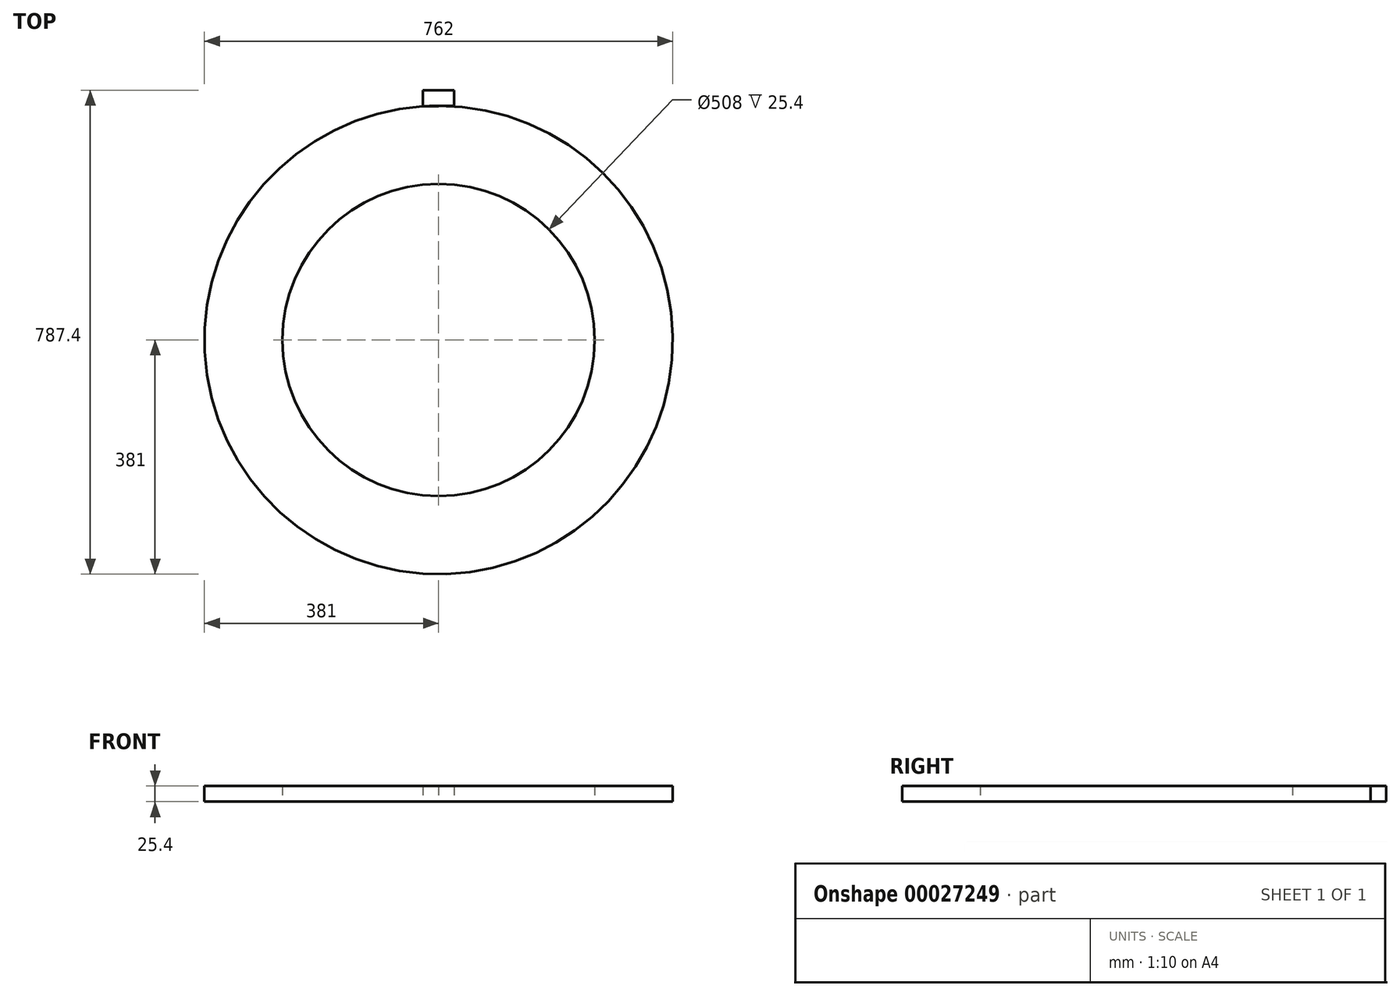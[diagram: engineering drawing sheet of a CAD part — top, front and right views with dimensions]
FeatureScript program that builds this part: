
annotation { "Feature Type Name" : "Feature", "Feature Type Description" : "" }
export const myFeature = defineFeature(function(context is Context, id is Id, definition is map)
    precondition{}
    {
        {
            var Q0;
            Q0=qCreatedBy(makeId("Top.planeOp"),FACE);
            var sketch = newSketch(context, id + "F0", { "sketchPlane" : qUnion([Q0])});
            skCircle(sketch, "E0", {"center": v(0, 0) * mm, "radius": 254 * mm});
            skCircle(sketch, "E1", {"center": v(0, 0) * mm, "radius": 381 * mm});
            skLineSegment(sketch, "E2", {"start": v(0, 0) * mm, "end": v(0, 430.5) * mm});
            skLineSegment(sketch, "E3.bottom", {"start": v(0, 381) * mm, "end": v(25.4, 381) * mm});
            skLineSegment(sketch, "E3.top", {"start": v(0, 406.4) * mm, "end": v(25.4, 406.4) * mm});
            skLineSegment(sketch, "E3.left", {"start": v(0, 381) * mm, "end": v(0, 406.4) * mm});
            skLineSegment(sketch, "E3.right", {"start": v(25.4, 381) * mm, "end": v(25.4, 406.4) * mm});
            skLineSegment(sketch, "E4.bottom", {"start": v(0, 381) * mm, "end": v(0, 381) * mm});
            skLineSegment(sketch, "E4.top", {"start": v(0, 406.4) * mm, "end": v(0, 406.4) * mm});
            skLineSegment(sketch, "E5.bottom", {"start": v(0, 406.4) * mm, "end": v(-25.4, 406.4) * mm});
            skLineSegment(sketch, "E5.top", {"start": v(0, 380.15) * mm, "end": v(-25.4, 380.15) * mm});
            skLineSegment(sketch, "E5.left", {"start": v(0, 406.4) * mm, "end": v(0, 380.15) * mm});
            skLineSegment(sketch, "E5.right", {"start": v(-25.4, 406.4) * mm, "end": v(-25.4, 380.15) * mm});
            skSolve(sketch);
        }
        {
            var Q0;
            Q0=makeQuery(id+"F0.imprint","IMPRINT",FACE,{"disambiguationData":[TD([[makeQuery(id+"F0.imprint","IMPRINT",EDGE,{"derivedFrom":sQuery(id+"F0.wireOp",EDGE,"E0")}),-1.0]])]});
            var Q1;
            {var subQ4=sQuery(id+"F0.wireOp",EDGE,"E5.bottom");Q1=makeQuery(id+"F0.imprint","IMPRINT",FACE,{"disambiguationData":[TD([[makeQuery(id+"F0.imprint","IMPRINT",EDGE,{"derivedFrom":subQ4}),1.0]])]});}
            var Q2;
            {var subQ0=sQuery(id+"F0.wireOp",EDGE,"E3.bottom");Q2=makeQuery(id+"F0.imprint","IMPRINT",FACE,{"disambiguationData":[TD([[makeQuery(id+"F0.imprint","IMPRINT",EDGE,{"derivedFrom":subQ0}),1.0]])]});}
            extrude(context, id + "F1", {"entities" : qUnion([Q0, Q1, Q2]), "depth" : 25.4 * mm});
        }
    });
